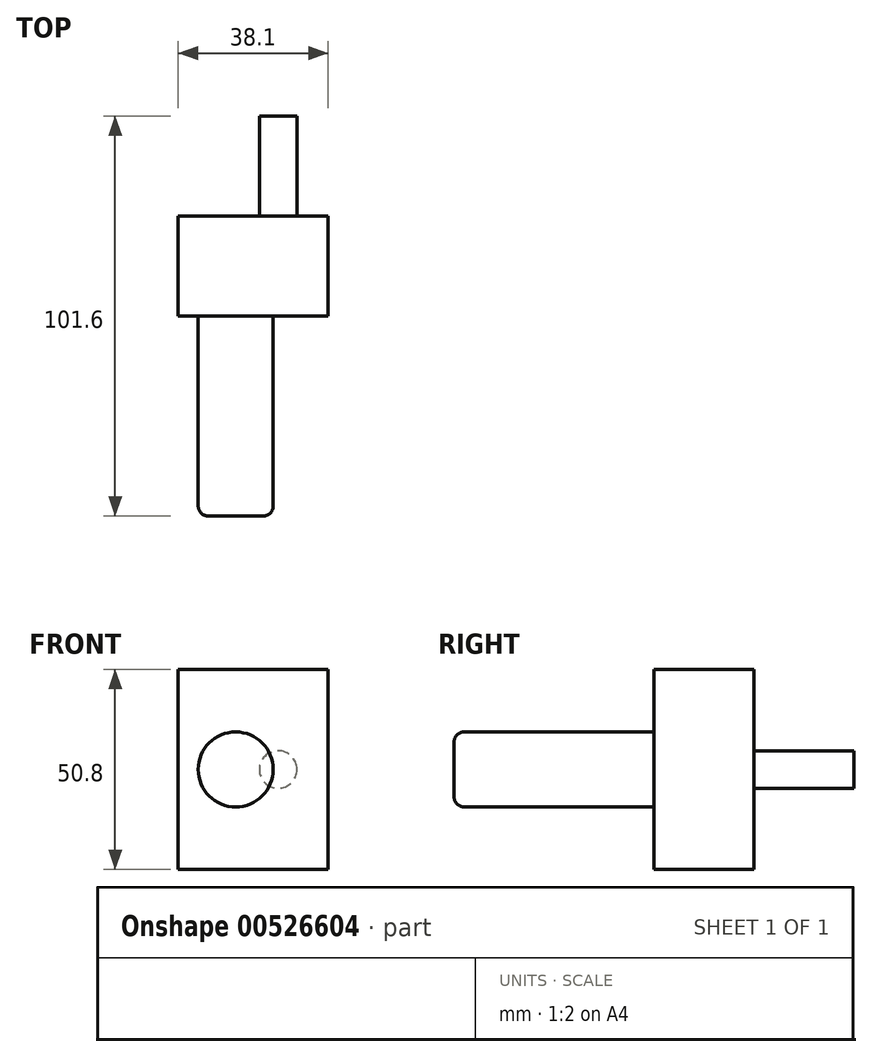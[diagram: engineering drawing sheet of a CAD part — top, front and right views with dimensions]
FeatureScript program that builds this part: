
annotation { "Feature Type Name" : "Feature", "Feature Type Description" : "" }
export const myFeature = defineFeature(function(context is Context, id is Id, definition is map)
    precondition{}
    {
        {
            var Q0;
            Q0=qCreatedBy(makeId("Front.planeOp"),FACE);
            var sketch = newSketch(context, id + "F0", { "sketchPlane" : qUnion([Q0])});
            skLineSegment(sketch, "E0.bottom", {"start": v(0, 0) * mm, "end": v(38.1, 0) * mm});
            skLineSegment(sketch, "E0.top", {"start": v(0, 50.8) * mm, "end": v(38.1, 50.8) * mm});
            skLineSegment(sketch, "E0.left", {"start": v(0, 0) * mm, "end": v(0, 50.8) * mm});
            skLineSegment(sketch, "E0.right", {"start": v(38.1, 0) * mm, "end": v(38.1, 50.8) * mm});
            skSolve(sketch);
        }
        {
            var Q0;
            Q0 = qSketchRegion(id + "F0", true);
            extrude(context, id + "F1", {"entities" : qUnion([Q0]), "depth" : 25.4 * mm, "offsetDistance" : 25.4 * mm});
        }
        {
            var Q0;
            Q0=makeQuery(id+"F1.opExtrude","CAP_FACE",FACE,{"disambiguationData":[OSD([sQuery(id+"F0.wireOp",EDGE,"E0.bottom"),sQuery(id+"F0.wireOp",EDGE,"E0.top"),sQuery(id+"F0.wireOp",EDGE,"E0.left"),sQuery(id+"F0.wireOp",EDGE,"E0.right")])],"isStart":false});
            var sketch = newSketch(context, id + "F2", { "sketchPlane" : qUnion([Q0])});
            skCircle(sketch, "E1", {"center": v(14.61, 25.4) * mm, "radius": 9.53 * mm});
            skPoint(sketch, "E1.centerSnap0", {"position": v(0, 25.4) * mm});
            skSolve(sketch);
        }
        {
            var Q0;
            Q0 = qSketchRegion(id + "F2", true);
            extrude(context, id + "F3", {"entities" : qUnion([Q0]), "operationType" : NewBodyOperationType.ADD, "depth" : 50.8 * mm, "offsetDistance" : 25.4 * mm});
        }
        {
            var Q0;
            Q0=makeQuery(id+"F3.opExtrude","CAP_EDGE",EDGE,{"disambiguationData":[OSD([sQuery(id+"F2.wireOp",EDGE,"E1")])],"isStart":false});
            fillet(context, id + "F4", {"entities" : qUnion([Q0]), "radius" : 2.54 * mm, "tangentPropagation" : true, "allowEdgeOverflow" : false});
        }
        {
            var Q0;
            Q0=makeQuery(id+"F0.imprint","IMPRINT",FACE,{"disambiguationData":[TD([[makeQuery(id+"F0.imprint","IMPRINT",EDGE,{"derivedFrom":sQuery(id+"F0.wireOp",EDGE,"E0.bottom")}),1.0]])]});
            var sketch = newSketch(context, id + "F5", { "sketchPlane" : qUnion([Q0])});
            skSolve(sketch);
        }
        {
            var Q0;
            Q0=makeQuery(id+"F5.imprint","IMPRINT",FACE,{"disambiguationData":[TD([[makeQuery(id+"F5.imprint","IMPRINT",EDGE,{"derivedFrom":makeQuery(id+"F0.imprint","IMPRINT",EDGE,{"derivedFrom":sQuery(id+"F0.wireOp",EDGE,"E0.bottom")})}),1.0]])]});
            var sketch = newSketch(context, id + "F6", { "sketchPlane" : qUnion([Q0])});
            skCircle(sketch, "E2", {"center": v(25.4, 25.4) * mm, "radius": 4.76 * mm});
            skSolve(sketch);
        }
        {
            var Q0;
            Q0 = qSketchRegion(id + "F6", true);
            extrude(context, id + "F7", {"entities" : qUnion([Q0]), "operationType" : NewBodyOperationType.ADD, "oppositeDirection" : true, "depth" : 25.4 * mm, "offsetDistance" : 25.4 * mm});
        }
    });
